# Revit family: Ворота распашные_PROM_UL_FENCE
name_source: partatom
category: Специальное оборудование
units: mm (PartAtom-declared; Revit-internal decimal feet)

## family parameters
Всегда вертикально = Да
На основе рабочей плоскости = Нет
Общий = Нет
При загрузке вырезать с полостями = Нет
Размер круглого соединителя = Использовать диаметр
Тип детали = Нормальный
Точка расчета площади = Нет

## types (4) — shared parameters
ADSK_Единица измерения = шт.
ADSK_Завод-изготовитель = FENSYS
ADSK_Комплект = Ворота распашные
URL = https://www.fensys.ru
Изготовитель = FENSYS
Материал_Сетка = FENSYS_Сетка_50x100
Материал_Столбы = FENSYS_Столб
Сечение столба = 80 мм
Таблица = UL_FENCE
Ширина рамки = 60 мм

## per-type parameters (varying)
| type | ADSK_Обозначение | Бетонирование в кондукторе (SIC) | Бетонирование столбы (SI) | Глубина столба | Тип крепления | Фланец (SIT) | Фланец под винтовую опору (SITgs) |
| PROM-UL_Под бетонирование | UL/SI/FENCE | Нет | Да | 500 мм | 2 | Нет | Нет |
| PROM-UL_Фланец | UL/SIT/FENCE | Нет | Нет | 0 мм | 3 | Да | Нет |
| PROM-UL_Фланец под винтовую опору | UL/SITgs/FENCE | Нет | Нет | 0 мм | 4 | Нет | Да |
| PROM-UL_Бетонирование в кондукторе | UL/SIC/FENCE | Да | Нет | 500 мм | 1 | Нет | Нет |
